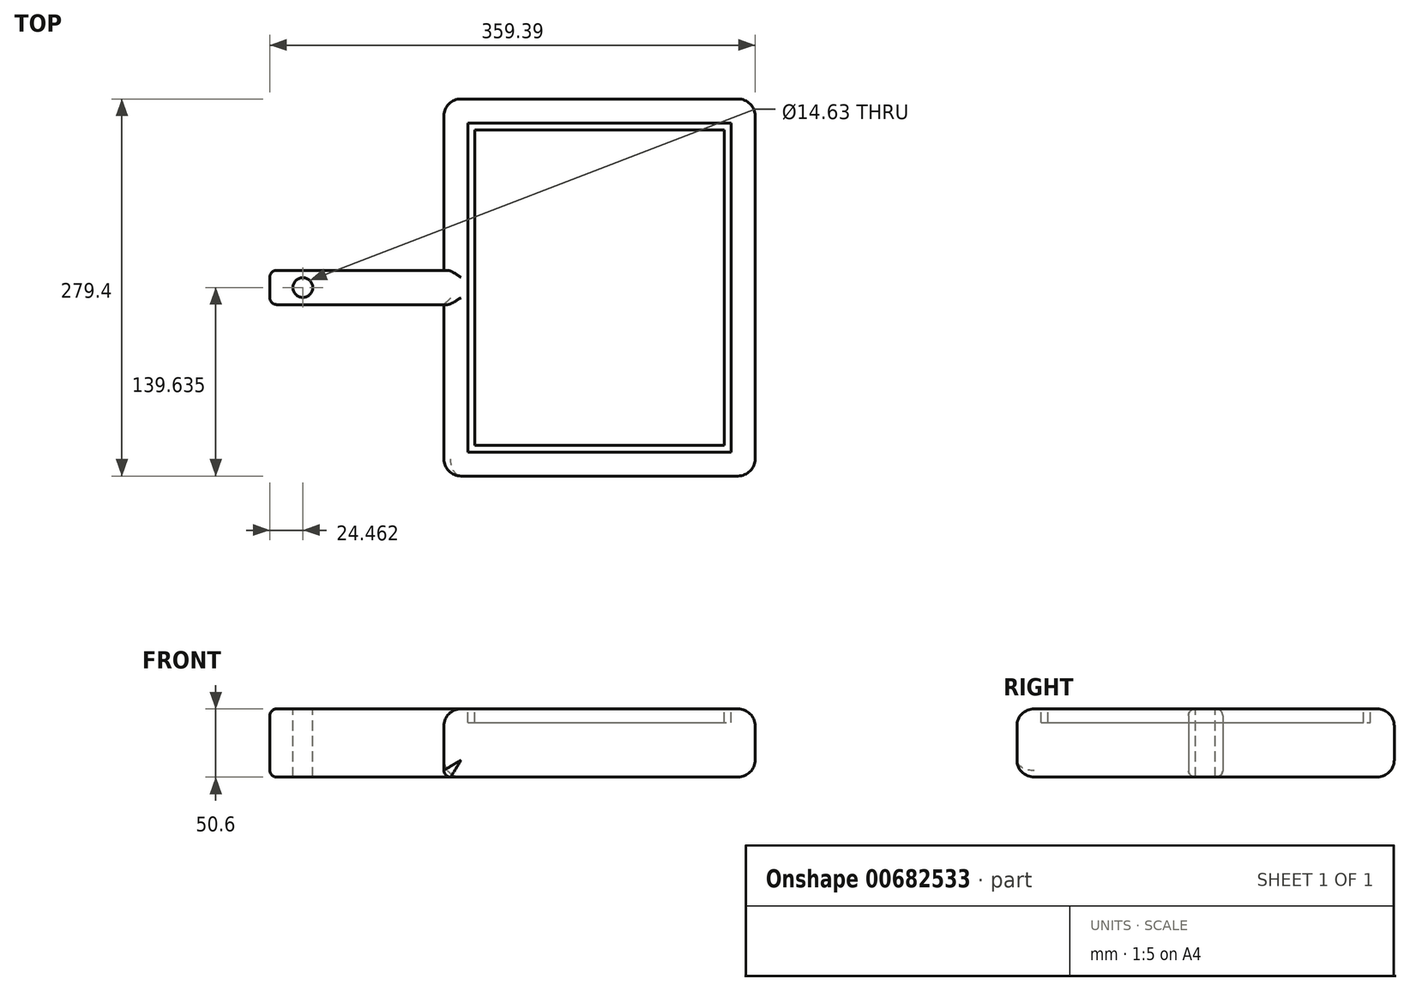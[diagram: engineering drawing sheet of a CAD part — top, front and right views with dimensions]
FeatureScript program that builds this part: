
annotation { "Feature Type Name" : "Feature", "Feature Type Description" : "" }
export const myFeature = defineFeature(function(context is Context, id is Id, definition is map)
    precondition{}
    {
        {
            var Q0;
            Q0=qCreatedBy(makeId("Front.planeOp"),FACE);
            var sketch = newSketch(context, id + "F0", { "sketchPlane" : qUnion([Q0])});
            skLineSegment(sketch, "E0", {"start": v(-99.83, 66.57) * mm, "end": v(157.96, 66.57) * mm});
            skLineSegment(sketch, "E1", {"start": v(-99.83, 66.57) * mm, "end": v(-99.83, 15.97) * mm});
            skLineSegment(sketch, "E2", {"start": v(-99.83, 15.97) * mm, "end": v(157.96, 15.97) * mm});
            skLineSegment(sketch, "E3", {"start": v(157.96, 66.57) * mm, "end": v(157.96, 15.97) * mm});
            skSolve(sketch);
        }
        {
            var Q0;
            Q0=makeQuery(id+"F0.imprint","IMPRINT",FACE,{"disambiguationData":[TD([[makeQuery(id+"F0.imprint","IMPRINT",EDGE,{"derivedFrom":sQuery(id+"F0.wireOp",EDGE,"E0")}),-1.0]])]});
            extrude(context, id + "F1", {"entities" : qUnion([Q0]), "depth" : 25.4 * mm, "offsetDistance" : 25.4 * mm});
        }
        {
            var Q0;
            Q0=makeQuery(id+"F1.opExtrude","CAP_FACE",FACE,{"disambiguationData":[OSD([sQuery(id+"F0.wireOp",EDGE,"E0"),sQuery(id+"F0.wireOp",EDGE,"E1"),sQuery(id+"F0.wireOp",EDGE,"E2"),sQuery(id+"F0.wireOp",EDGE,"E3")])],"isStart":false});
            var sketch = newSketch(context, id + "F2", { "sketchPlane" : qUnion([Q0])});
            skLineSegment(sketch, "E4", {"start": v(29.07, 66.57) * mm, "end": v(29.07, 15.97) * mm});
            skLineSegment(sketch, "E5", {"start": v(29.07, 15.97) * mm, "end": v(157.96, 15.97) * mm});
            skLineSegment(sketch, "E6", {"start": v(157.96, 15.97) * mm, "end": v(157.96, 66.57) * mm});
            skLineSegment(sketch, "E7", {"start": v(157.96, 66.57) * mm, "end": v(29.07, 66.57) * mm});
            skSolve(sketch);
        }
        {
            var Q0;
            Q0=makeQuery(id+"F2.imprint","IMPRINT",FACE,{"disambiguationData":[TD([[makeQuery(id+"F2.imprint","IMPRINT",EDGE,{"derivedFrom":sQuery(id+"F2.wireOp",EDGE,"E4")}),1.0]])]});
            extrude(context, id + "F3", {"entities" : qUnion([Q0]), "operationType" : NewBodyOperationType.ADD, "depth" : 127 * mm, "offsetDistance" : 25.4 * mm});
        }
        {
            var Q0;
            Q0=makeQuery(id+"F3.boolean.opBoolean","MERGE",FACE,{"derivedFrom":[makeQuery(id+"F1.opExtrude","SWEPT_FACE",FACE,{"disambiguationData":[OSD([sQuery(id+"F0.wireOp",EDGE,"E0")])]}),makeQuery(id+"F3.opExtrude","SWEPT_FACE",FACE,{"disambiguationData":[OSD([sQuery(id+"F2.wireOp",EDGE,"E7")])]})]});
            var sketch = newSketch(context, id + "F4", { "sketchPlane" : qUnion([Q0])});
            skLineSegment(sketch, "E8", {"start": v(29.07, -25.4) * mm, "end": v(29.07, 0) * mm});
            skSolve(sketch);
        }
        {
            var Q0;
            Q0=makeQuery(id+"F1.opExtrude","CAP_FACE",FACE,{"disambiguationData":[OSD([sQuery(id+"F0.wireOp",EDGE,"E0"),sQuery(id+"F0.wireOp",EDGE,"E1"),sQuery(id+"F0.wireOp",EDGE,"E2"),sQuery(id+"F0.wireOp",EDGE,"E3")])],"isStart":true});
            var sketch = newSketch(context, id + "F5", { "sketchPlane" : qUnion([Q0])});
            skLineSegment(sketch, "E9", {"start": v(-29.07, 66.57) * mm, "end": v(-29.07, 15.97) * mm});
            skLineSegment(sketch, "E10", {"start": v(-29.07, 15.97) * mm, "end": v(-157.96, 15.97) * mm});
            skLineSegment(sketch, "E11", {"start": v(-157.96, 15.97) * mm, "end": v(-157.96, 66.57) * mm});
            skLineSegment(sketch, "E12", {"start": v(-157.96, 66.57) * mm, "end": v(-29.07, 66.57) * mm});
            skSolve(sketch);
        }
        {
            var Q0;
            Q0=makeQuery(id+"F5.imprint","IMPRINT",FACE,{"disambiguationData":[TD([[makeQuery(id+"F5.imprint","IMPRINT",EDGE,{"derivedFrom":sQuery(id+"F5.wireOp",EDGE,"E9")}),-1.0]])]});
            extrude(context, id + "F6", {"entities" : qUnion([Q0]), "operationType" : NewBodyOperationType.ADD, "depth" : 127 * mm, "offsetDistance" : 25.4 * mm});
        }
        {
            var Q0;
            Q0=makeQuery(id+"F6.boolean.opBoolean","MERGE",FACE,{"derivedFrom":[makeQuery(id+"F3.boolean.opBoolean","MERGE",FACE,{"derivedFrom":[makeQuery(id+"F1.opExtrude","SWEPT_FACE",FACE,{"disambiguationData":[OSD([sQuery(id+"F0.wireOp",EDGE,"E3")])]}),makeQuery(id+"F3.opExtrude","SWEPT_FACE",FACE,{"disambiguationData":[OSD([sQuery(id+"F2.wireOp",EDGE,"E6")])]})]}),makeQuery(id+"F6.opExtrude","SWEPT_FACE",FACE,{"disambiguationData":[OSD([sQuery(id+"F5.wireOp",EDGE,"E11")])]})]});
            extrude(context, id + "F7", {"entities" : qUnion([Q0]), "operationType" : NewBodyOperationType.ADD, "depth" : 101.6 * mm, "offsetDistance" : 25.4 * mm});
        }
        {
            var Q0;
            {var subQ0=sQuery(id+"F4.wireOp",EDGE,"E8");Q0=makeQuery(id+"F4.imprint","IMPRINT",FACE,{"disambiguationData":[TD([[makeQuery(id+"F4.imprint","IMPRINT",EDGE,{"derivedFrom":subQ0}),1.0]])]});}
            var sketch = newSketch(context, id + "F8", { "sketchPlane" : qUnion([Q0])});
            skLineSegment(sketch, "E13", {"start": v(-75.37, -25.53) * mm, "end": v(-75.37, 0) * mm});
            skCircle(sketch, "E14", {"center": v(-75.37, -12.77) * mm, "radius": 7.32 * mm});
            skSolve(sketch);
        }
        {
            var Q0;
            {var subQ0=sQuery(id+"F8.wireOp",EDGE,"E14");var subQ1=sQuery(id+"F8.wireOp",EDGE,"E13");var subQ2=makeQuery(id+"F8.imprint","INTERSECT",VERTEX,{"disambiguationData":[OD(0.0)],"derivedFrom":[subQ1,subQ0]});Q0=makeQuery(id+"F8.imprint","IMPRINT",FACE,{"disambiguationData":[TD([[makeQuery(id+"F8.imprint","IMPRINT",EDGE,{"disambiguationData":[TD([[subQ2,-1.0]])],"derivedFrom":subQ1}),1.0]])]});}
            var Q1;
            {var subQ0=sQuery(id+"F8.wireOp",EDGE,"E14");var subQ1=sQuery(id+"F8.wireOp",EDGE,"E13");var subQ2=makeQuery(id+"F8.imprint","INTERSECT",VERTEX,{"disambiguationData":[OD(0.0)],"derivedFrom":[subQ1,subQ0]});Q1=makeQuery(id+"F8.imprint","IMPRINT",FACE,{"disambiguationData":[TD([[makeQuery(id+"F8.imprint","IMPRINT",EDGE,{"disambiguationData":[TD([[subQ2,-1.0]])],"derivedFrom":subQ1}),-1.0]])]});}
            extrude(context, id + "F9", {"entities" : qUnion([Q0, Q1]), "operationType" : NewBodyOperationType.REMOVE, "endBound" : BoundingType.THROUGH_ALL, "oppositeDirection" : true, "depth" : 25.4 * mm, "offsetDistance" : 25.4 * mm});
        }
        {
            var Q0;
            Q0=makeQuery(id+"F1.opExtrude","CAP_EDGE",EDGE,{"disambiguationData":[OSD([sQuery(id+"F0.wireOp",EDGE,"E0")])],"isStart":false});
            var Q1;
            Q1=makeQuery(id+"F1.opExtrude","SWEPT_EDGE",EDGE,{"disambiguationData":[OSD([sQuery(id+"F0.wireOp",EDGE,"E0"),sQuery(id+"F0.wireOp",EDGE,"E1")])]});
            var Q2;
            Q2=makeQuery(id+"F1.opExtrude","CAP_EDGE",EDGE,{"disambiguationData":[OSD([sQuery(id+"F0.wireOp",EDGE,"E0")])],"isStart":true});
            var Q3;
            Q3=makeQuery(id+"F1.opExtrude","CAP_EDGE",EDGE,{"disambiguationData":[OSD([sQuery(id+"F0.wireOp",EDGE,"E1")])],"isStart":false});
            var Q4;
            Q4=makeQuery(id+"F1.opExtrude","CAP_EDGE",EDGE,{"disambiguationData":[OSD([sQuery(id+"F0.wireOp",EDGE,"E1")])],"isStart":true});
            var Q5;
            Q5=makeQuery(id+"F1.opExtrude","CAP_EDGE",EDGE,{"disambiguationData":[OSD([sQuery(id+"F0.wireOp",EDGE,"E2")])],"isStart":true});
            var Q6;
            Q6=makeQuery(id+"F1.opExtrude","SWEPT_EDGE",EDGE,{"disambiguationData":[OSD([sQuery(id+"F0.wireOp",EDGE,"E1"),sQuery(id+"F0.wireOp",EDGE,"E2")])]});
            var Q7;
            Q7=makeQuery(id+"F1.opExtrude","CAP_EDGE",EDGE,{"disambiguationData":[OSD([sQuery(id+"F0.wireOp",EDGE,"E2")])],"isStart":false});
            fillet(context, id + "F10", {"entities" : qUnion([Q0, Q1, Q2, Q3, Q4, Q5, Q6, Q7]), "radius" : 5.08 * mm, "tangentPropagation" : true, "allowEdgeOverflow" : false});
        }
        {
            var Q0;
            Q0=makeQuery(id+"F7.opExtrude","CAP_EDGE",EDGE,{"disambiguationData":[OSD([sQuery(id+"F0.wireOp",EDGE,"E0"),sQuery(id+"F0.wireOp",EDGE,"E3"),sQuery(id+"F2.wireOp",EDGE,"E6"),sQuery(id+"F2.wireOp",EDGE,"E7"),sQuery(id+"F5.wireOp",EDGE,"E11"),sQuery(id+"F5.wireOp",EDGE,"E12")])],"isStart":false});
            var Q1;
            {var subQ0=sQuery(id+"F5.wireOp",EDGE,"E12");Q1=makeQuery(id+"F7.boolean.opBoolean","MERGE",EDGE,{"derivedFrom":[makeQuery(id+"F6.opExtrude","CAP_EDGE",EDGE,{"disambiguationData":[OSD([subQ0])],"isStart":false}),makeQuery(id+"F7.opExtrude","SWEPT_EDGE",EDGE,{"disambiguationData":[OSD([sQuery(id+"F5.wireOp",EDGE,"E11"),subQ0])]})]});}
            var Q2;
            Q2=makeQuery(id+"F6.opExtrude","SWEPT_EDGE",EDGE,{"disambiguationData":[OSD([sQuery(id+"F0.wireOp",EDGE,"E0"),sQuery(id+"F5.wireOp",EDGE,"E9"),sQuery(id+"F5.wireOp",EDGE,"E12")])]});
            var Q3;
            Q3=makeQuery(id+"F6.opExtrude","SWEPT_EDGE",EDGE,{"disambiguationData":[OSD([sQuery(id+"F0.wireOp",EDGE,"E2"),sQuery(id+"F5.wireOp",EDGE,"E9"),sQuery(id+"F5.wireOp",EDGE,"E10")])]});
            var Q4;
            Q4=makeQuery(id+"F6.opExtrude","CAP_EDGE",EDGE,{"disambiguationData":[OSD([sQuery(id+"F5.wireOp",EDGE,"E9")])],"isStart":false});
            var Q5;
            Q5=makeQuery(id+"F7.opExtrude","CAP_EDGE",EDGE,{"disambiguationData":[OSD([sQuery(id+"F5.wireOp",EDGE,"E11")])],"isStart":false});
            var Q6;
            {var subQ0=sQuery(id+"F5.wireOp",EDGE,"E10");Q6=makeQuery(id+"F7.boolean.opBoolean","MERGE",EDGE,{"derivedFrom":[makeQuery(id+"F6.opExtrude","CAP_EDGE",EDGE,{"disambiguationData":[OSD([subQ0])],"isStart":false}),makeQuery(id+"F7.opExtrude","SWEPT_EDGE",EDGE,{"disambiguationData":[OSD([subQ0,sQuery(id+"F5.wireOp",EDGE,"E11")])]})]});}
            var Q7;
            Q7=makeQuery(id+"F7.opExtrude","CAP_EDGE",EDGE,{"disambiguationData":[OSD([sQuery(id+"F0.wireOp",EDGE,"E2"),sQuery(id+"F0.wireOp",EDGE,"E3"),sQuery(id+"F2.wireOp",EDGE,"E5"),sQuery(id+"F2.wireOp",EDGE,"E6"),sQuery(id+"F5.wireOp",EDGE,"E10"),sQuery(id+"F5.wireOp",EDGE,"E11")])],"isStart":false});
            var Q8;
            {var subQ0=sQuery(id+"F2.wireOp",EDGE,"E5");Q8=makeQuery(id+"F7.boolean.opBoolean","MERGE",EDGE,{"derivedFrom":[makeQuery(id+"F3.opExtrude","CAP_EDGE",EDGE,{"disambiguationData":[OSD([subQ0])],"isStart":false}),makeQuery(id+"F7.opExtrude","SWEPT_EDGE",EDGE,{"disambiguationData":[OSD([subQ0,sQuery(id+"F2.wireOp",EDGE,"E6")])]})]});}
            var Q9;
            Q9=makeQuery(id+"F7.opExtrude","CAP_EDGE",EDGE,{"disambiguationData":[OSD([sQuery(id+"F2.wireOp",EDGE,"E6")])],"isStart":false});
            var Q10;
            {var subQ0=sQuery(id+"F2.wireOp",EDGE,"E7");Q10=makeQuery(id+"F7.boolean.opBoolean","MERGE",EDGE,{"derivedFrom":[makeQuery(id+"F3.opExtrude","CAP_EDGE",EDGE,{"disambiguationData":[OSD([subQ0])],"isStart":false}),makeQuery(id+"F7.opExtrude","SWEPT_EDGE",EDGE,{"disambiguationData":[OSD([sQuery(id+"F2.wireOp",EDGE,"E6"),subQ0])]})]});}
            var Q11;
            Q11=makeQuery(id+"F3.opExtrude","CAP_EDGE",EDGE,{"disambiguationData":[OSD([sQuery(id+"F2.wireOp",EDGE,"E4")])],"isStart":false});
            var Q12;
            Q12=makeQuery(id+"F3.opExtrude","CAP_EDGE",EDGE,{"disambiguationData":[OSD([sQuery(id+"F2.wireOp",EDGE,"E4")])],"isStart":true});
            var Q13;
            Q13=makeQuery(id+"F6.opExtrude","CAP_EDGE",EDGE,{"disambiguationData":[OSD([sQuery(id+"F5.wireOp",EDGE,"E9")])],"isStart":true});
            var Q14;
            Q14=makeQuery(id+"F3.opExtrude","SWEPT_EDGE",EDGE,{"disambiguationData":[OSD([sQuery(id+"F0.wireOp",EDGE,"E0"),sQuery(id+"F2.wireOp",EDGE,"E4"),sQuery(id+"F2.wireOp",EDGE,"E7")])]});
            fillet(context, id + "F11", {"entities" : qUnion([Q0, Q1, Q2, Q3, Q4, Q5, Q6, Q7, Q8, Q9, Q10, Q11, Q12, Q13, Q14]), "radius" : 12.7 * mm, "tangentPropagation" : true, "allowEdgeOverflow" : false});
        }
        {
            var Q0;
            {var subQ3=sQuery(id+"F4.wireOp",EDGE,"E8");Q0=makeQuery(id+"F4.imprint","IMPRINT",FACE,{"disambiguationData":[TD([[makeQuery(id+"F4.imprint","IMPRINT",EDGE,{"derivedFrom":subQ3}),-1.0]])]});}
            var sketch = newSketch(context, id + "F12", { "sketchPlane" : qUnion([Q0])});
            skLineSegment(sketch, "E15.bottom", {"start": v(46.85, -134.62) * mm, "end": v(241.78, -134.62) * mm});
            skLineSegment(sketch, "E15.top", {"start": v(46.85, 109.22) * mm, "end": v(241.78, 109.22) * mm});
            skLineSegment(sketch, "E15.left", {"start": v(46.85, -134.62) * mm, "end": v(46.85, 109.22) * mm});
            skLineSegment(sketch, "E15.right", {"start": v(241.78, -134.62) * mm, "end": v(241.78, 109.22) * mm});
            skLineSegment(sketch, "E16.bottom", {"start": v(51.93, -129.54) * mm, "end": v(236.7, -129.54) * mm});
            skLineSegment(sketch, "E16.top", {"start": v(51.93, 104.14) * mm, "end": v(236.7, 104.14) * mm});
            skLineSegment(sketch, "E16.left", {"start": v(51.93, -129.54) * mm, "end": v(51.93, 104.14) * mm});
            skLineSegment(sketch, "E16.right", {"start": v(236.7, -129.54) * mm, "end": v(236.7, 104.14) * mm});
            skSolve(sketch);
        }
        {
            var Q0;
            {var subQ2=sQuery(id+"F12.wireOp",EDGE,"E15.top");Q0=makeQuery(id+"F12.imprint","IMPRINT",FACE,{"disambiguationData":[TD([[makeQuery(id+"F12.imprint","IMPRINT",EDGE,{"derivedFrom":subQ2}),-1.0]])]});}
            var Q1;
            {var subQ8=sQuery(id+"F12.wireOp",EDGE,"E15.left");var subQ12=sQuery(id+"F12.wireOp",EDGE,"E15.bottom");var subQ14=makeQuery(id+"F12.imprint","INTERSECT",VERTEX,{"derivedFrom":[subQ12,subQ8]});Q1=makeQuery(id+"F12.imprint","IMPRINT",FACE,{"disambiguationData":[TD([[makeQuery(id+"F12.imprint","IMPRINT",EDGE,{"disambiguationData":[TD([[subQ14,-1.0]])],"derivedFrom":subQ12}),1.0]])]});}
            extrude(context, id + "F13", {"entities" : qUnion([Q0, Q1]), "operationType" : NewBodyOperationType.REMOVE, "oppositeDirection" : true, "depth" : 10.16 * mm, "offsetDistance" : 25.4 * mm});
        }
        {
            var Q0;
            Q0=makeQuery(id+"F3.opExtrude","SWEPT_EDGE",EDGE,{"disambiguationData":[OSD([sQuery(id+"F0.wireOp",EDGE,"E2"),sQuery(id+"F2.wireOp",EDGE,"E4"),sQuery(id+"F2.wireOp",EDGE,"E5")])]});
            fillet(context, id + "F14", {"entities" : qUnion([Q0]), "radius" : 5.08 * mm, "tangentPropagation" : true, "allowEdgeOverflow" : false});
        }
    });
